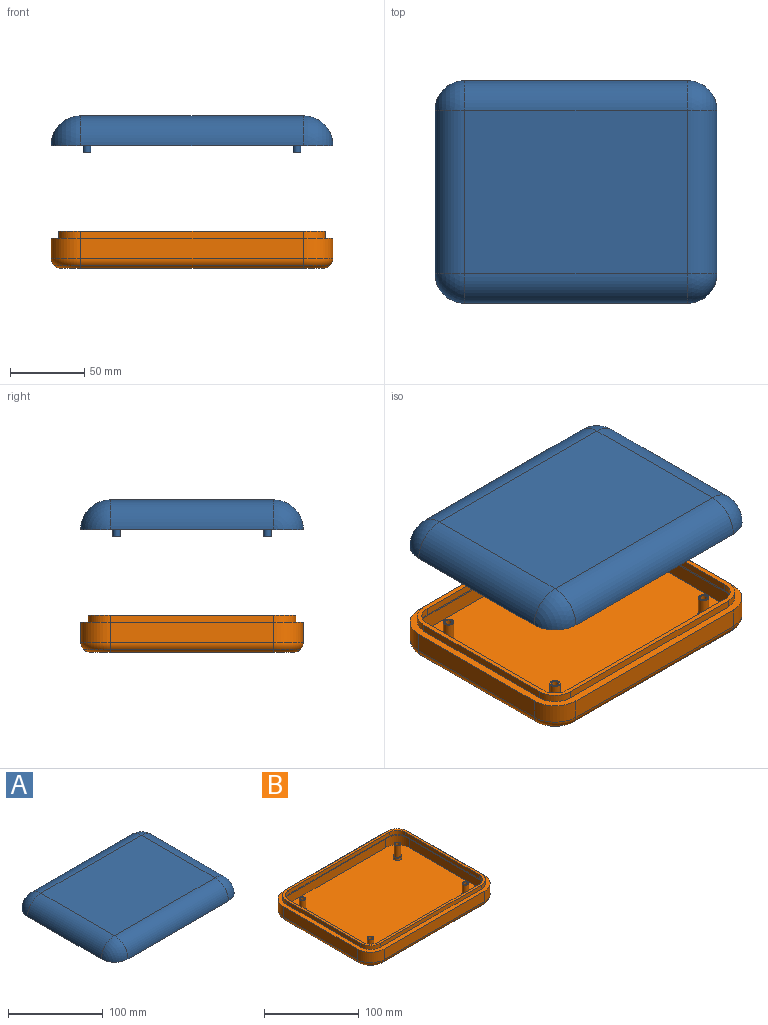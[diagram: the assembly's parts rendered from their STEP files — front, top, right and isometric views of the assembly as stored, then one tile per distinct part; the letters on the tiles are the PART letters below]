
ASSEMBLY  parts=2 mates=1
PART A: 43 faces, bbox 190x150x25 mm
  f0: plane 150x110mm, normal (0,0,-1), area 16346.1mm2, adj f3,f10,f16,f18,f19,f21,f23,f25
  f1: plane 150x110mm, normal (0,0,1), area 16500mm2, adj f6,f13,f15,f17
  f2: sphere r=15mm, area 353.4mm2, adj f3,f8,f16
  f3: cylinder r=15mm len=150mm, axis (-1,0,0), area 3534.3mm2, adj f0,f2,f4,f8
  f4: sphere r=15mm, area 353.4mm2, adj f3,f8,f18
  f5: sphere r=20mm, area 628.3mm2, adj f6,f8,f17
  f6: cylinder r=20mm len=150mm, axis (-1,0,0), area 4712.4mm2, adj f1,f5,f7,f8
  f7: sphere r=20mm, area 628.3mm2, adj f6,f8,f15
  f8: plane 190x150mm, normal (0,0,-1), area 3149.8mm2, adj f2,f3,f4,f5,f6,f7,f9,f10
  f9: sphere r=15mm, area 353.4mm2, adj f8,f10,f18
  f10: cylinder r=15mm len=150mm, axis (1,0,0), area 3534.3mm2, adj f0,f8,f9,f11
  f11: sphere r=15mm, area 353.4mm2, adj f8,f10,f16
  f12: sphere r=20mm, area 628.3mm2, adj f8,f13,f15
  f13: cylinder r=20mm len=150mm, axis (1,0,0), area 4712.4mm2, adj f1,f8,f12,f14
  f14: sphere r=20mm, area 628.3mm2, adj f8,f13,f17
  f15: cylinder r=20mm len=110mm, axis (0,1,0), area 3455.8mm2, adj f1,f7,f8,f12
  f16: cylinder r=15mm len=110mm, axis (0,1,0), area 2591.8mm2, adj f0,f2,f8,f11
  f17: cylinder r=20mm len=110mm, axis (0,-1,0), area 3455.8mm2, adj f1,f5,f8,f14
  f18: cylinder r=15mm len=110mm, axis (0,-1,0), area 2591.8mm2, adj f0,f4,f8,f9
  f19: cylinder r=3.5mm len=15mm, axis (0,0,1), area 329.9mm2, adj f0,f20
  f20: plane 7x7mm, normal (0,0,-1), area 18.8mm2, adj f19,f27
  f21: cylinder r=3.5mm len=15mm, axis (0,0,1), area 329.9mm2, adj f0,f22
  f22: plane 7x7mm, normal (0,0,-1), area 18.8mm2, adj f21,f32
  f23: cylinder r=3.5mm len=15mm, axis (0,0,1), area 329.9mm2, adj f0,f24
  f24: plane 7x7mm, normal (0,0,-1), area 18.8mm2, adj f23,f36
  f25: cylinder r=3.5mm len=15mm, axis (0,0,1), area 329.9mm2, adj f0,f26
  f26: plane 7x7mm, normal (0,0,-1), area 18.8mm2, adj f25,f40
  f27: cylinder r=2.5mm len=5mm, axis (0,0,1), area 78.5mm2, adj f20,f29
  f28: cylinder r=1.5mm len=20mm, axis (0,0,1), area 188.5mm2, adj f29,f30
  f29: plane 5x5mm, normal (0,0,-1), area 12.6mm2, adj f27,f28
  f30: plane 3x3mm, normal (0,0,-1), area 7.1mm2, adj f28
  f31: cylinder r=1.5mm len=20mm, axis (0,0,1), area 188.5mm2, adj f33,f34
  f32: cylinder r=2.5mm len=5mm, axis (0,0,1), area 78.5mm2, adj f22,f33
  f33: plane 5x5mm, normal (0,0,-1), area 12.6mm2, adj f31,f32
  f34: plane 3x3mm, normal (0,0,-1), area 7.1mm2, adj f31
  f35: cylinder r=1.5mm len=20mm, axis (0,0,1), area 188.5mm2, adj f37,f38
  f36: cylinder r=2.5mm len=5mm, axis (0,0,1), area 78.5mm2, adj f24,f37
  f37: plane 5x5mm, normal (0,0,-1), area 12.6mm2, adj f35,f36
  f38: plane 3x3mm, normal (0,0,-1), area 7.1mm2, adj f35
  f39: cylinder r=1.5mm len=20mm, axis (0,0,1), area 188.5mm2, adj f41,f42
  f40: cylinder r=2.5mm len=5mm, axis (0,0,1), area 78.5mm2, adj f26,f41
  f41: plane 5x5mm, normal (0,0,-1), area 12.6mm2, adj f39,f40
  f42: plane 3x3mm, normal (0,0,-1), area 7.1mm2, adj f39
PART B: 90 faces, bbox 193.3x153.3x25 mm
  f0: cylinder r=1.5mm len=12mm, axis (0,0,-1), area 113.1mm2, adj f35,f89
  f1: cylinder r=1.5mm len=12mm, axis (0,0,-1), area 113.1mm2, adj f37,f87
  f2: cylinder r=1.5mm len=12mm, axis (0,0,-1), area 113.1mm2, adj f39,f85
  f3: cylinder r=1.5mm len=12mm, axis (0,0,-1), area 113.1mm2, adj f41,f83
  f4: plane 7x7mm, normal (0,0,1), area 18.8mm2, adj f62,f88
  f5: plane 7x7mm, normal (0,0,1), area 18.8mm2, adj f65,f86
  f6: plane 7x7mm, normal (0,0,1), area 18.8mm2, adj f68,f84
  f7: plane 7x7mm, normal (0,0,1), area 18.8mm2, adj f71,f82
  f8: plane 190x150mm, normal (0,0,1), area 3149.8mm2, adj f9,f10,f11,f12,f13,f14,f15,f16
  f9: cylinder r=20mm len=20mm, axis (0,0,1), area 424.1mm2, adj f8,f10,f16,f79
  f10: plane 150x13.5mm, normal (0,-1,0), area 2025mm2, adj f8,f9,f11,f77
  f11: cylinder r=20mm len=20mm, axis (0,0,1), area 424.1mm2, adj f8,f10,f12,f75
  f12: plane 110x13.5mm, normal (1,0,0), area 1485mm2, adj f8,f11,f13,f74
  f13: cylinder r=20mm len=20mm, axis (0,0,1), area 424.1mm2, adj f8,f12,f14,f76
  f14: plane 150x13.5mm, normal (0,1,0), area 2025mm2, adj f8,f13,f15,f78
  f15: cylinder r=20mm len=20mm, axis (0,0,1), area 424.1mm2, adj f8,f14,f16,f80
  f16: plane 110x13.5mm, normal (-1,0,0), area 1485mm2, adj f8,f9,f15,f81
  f17: plane 177x137mm, normal (0,0,-1), area 24014mm2, adj f36,f38,f40,f42,f74,f75,f76,f77
  f18: plane 150x5mm, normal (0,1,0), area 750mm2, adj f19,f33,f34,f43
  f19: cylinder r=12mm len=12mm, axis (0,0,-1), area 94.2mm2, adj f18,f20,f34,f43
  f20: plane 110x5mm, normal (1,0,0), area 550mm2, adj f19,f21,f34,f43
  f21: cylinder r=12mm len=12mm, axis (0,0,-1), area 94.2mm2, adj f20,f22,f34,f43
  f22: plane 150x5mm, normal (0,-1,0), area 750mm2, adj f21,f23,f34,f43
  f23: cylinder r=12mm len=12mm, axis (0,0,-1), area 94.2mm2, adj f22,f24,f34,f43
  f24: plane 110x5mm, normal (-1,0,0), area 550mm2, adj f23,f33,f34,f43
  f25: cylinder r=15mm len=15mm, axis (0,0,-1), area 117.8mm2, adj f8,f26,f32,f34
  f26: plane 150x5mm, normal (0,-1,0), area 750mm2, adj f8,f25,f27,f34
  f27: cylinder r=15mm len=15mm, axis (0,0,-1), area 117.8mm2, adj f8,f26,f28,f34
  f28: plane 110x5mm, normal (1,0,0), area 550mm2, adj f8,f27,f29,f34
  f29: cylinder r=15mm len=15mm, axis (0,0,-1), area 117.8mm2, adj f8,f28,f30,f34
  f30: plane 150x5mm, normal (0,1,0), area 750mm2, adj f8,f29,f31,f34
  f31: cylinder r=15mm len=15mm, axis (0,0,-1), area 117.8mm2, adj f8,f30,f32,f34
  f32: plane 110x5mm, normal (-1,0,0), area 550mm2, adj f8,f25,f31,f34
  f33: cylinder r=12mm len=12mm, axis (0,0,-1), area 94.2mm2, adj f18,f24,f34,f43
  f34: plane 180x140mm, normal (0,0,1), area 1814.5mm2, adj f18,f19,f20,f21,f22,f23,f24,f25
  f35: plane 5x5mm, normal (0,0,-1), area 12.6mm2, adj f0,f36
  f36: cylinder r=2.5mm len=5mm, axis (0,0,-1), area 47.1mm2, adj f17,f35
  f37: plane 5x5mm, normal (0,0,-1), area 12.6mm2, adj f1,f38
  f38: cylinder r=2.5mm len=5mm, axis (0,0,-1), area 47.1mm2, adj f17,f37
  f39: plane 5x5mm, normal (0,0,-1), area 12.6mm2, adj f2,f40
  f40: cylinder r=2.5mm len=5mm, axis (0,0,-1), area 47.1mm2, adj f17,f39
  f41: plane 5x5mm, normal (0,0,-1), area 12.6mm2, adj f3,f42
  f42: cylinder r=2.5mm len=5mm, axis (0,0,-1), area 47.1mm2, adj f17,f41
  f43: plane 176x136mm, normal (0,0,-1), area 598.5mm2, adj f18,f19,f20,f21,f22,f23,f24,f33
  f44: plane 186x146mm, normal (0,0,-1), area 3086.9mm2, adj f45,f46,f47,f48,f49,f50,f51,f52
  f45: cylinder r=18mm len=18mm, axis (0,0,1), area 452.4mm2, adj f44,f46,f52,f53
  f46: plane 150x16mm, normal (0,1,0), area 2400mm2, adj f44,f45,f47,f53
  f47: cylinder r=18mm len=18mm, axis (0,0,1), area 452.4mm2, adj f44,f46,f48,f53
  f48: plane 110x16mm, normal (-1,0,0), area 1760mm2, adj f44,f47,f49,f53
  f49: cylinder r=18mm len=18mm, axis (0,0,1), area 452.4mm2, adj f44,f48,f50,f53
  f50: plane 150x16mm, normal (0,-1,0), area 2400mm2, adj f44,f49,f51,f53
  f51: cylinder r=18mm len=18mm, axis (0,0,1), area 452.4mm2, adj f44,f50,f52,f53
  f52: plane 110x16mm, normal (1,0,0), area 1760mm2, adj f44,f45,f51,f53
  f53: plane 186x146mm, normal (0,0,1), area 26623.4mm2, adj f45,f46,f47,f48,f49,f50,f51,f52
  f54: cylinder r=13mm len=13mm, axis (0,0,-1), area 40.8mm2, adj f43,f44,f55,f61
  f55: plane 150x2mm, normal (0,1,0), area 300mm2, adj f43,f44,f54,f56
  f56: cylinder r=13mm len=13mm, axis (0,0,-1), area 40.8mm2, adj f43,f44,f55,f57
  f57: plane 110x2mm, normal (-1,0,0), area 220mm2, adj f43,f44,f56,f58
  f58: cylinder r=13mm len=13mm, axis (0,0,-1), area 40.8mm2, adj f43,f44,f57,f59
  f59: plane 150x2mm, normal (0,-1,0), area 300mm2, adj f43,f44,f58,f60
  f60: cylinder r=13mm len=13mm, axis (0,0,-1), area 40.8mm2, adj f43,f44,f59,f61
  f61: plane 110x2mm, normal (1,0,0), area 220mm2, adj f43,f44,f54,f60
  f62: cylinder r=3.5mm len=15mm, axis (0,0,-1), area 329.9mm2, adj f4,f63
  f63: plane 9x9mm, normal (0,0,1), area 25.1mm2, adj f62,f64
  f64: cylinder r=4.5mm len=9mm, axis (0,0,-1), area 84.8mm2, adj f53,f63
  f65: cylinder r=3.5mm len=15mm, axis (0,0,-1), area 329.9mm2, adj f5,f66
  f66: plane 9x9mm, normal (0,0,1), area 25.1mm2, adj f65,f67
  f67: cylinder r=4.5mm len=9mm, axis (0,0,-1), area 84.8mm2, adj f53,f66
  f68: cylinder r=3.5mm len=15mm, axis (0,0,-1), area 329.9mm2, adj f6,f69
  f69: plane 9x9mm, normal (0,0,1), area 25.1mm2, adj f68,f70
  f70: cylinder r=4.5mm len=9mm, axis (0,0,-1), area 84.8mm2, adj f53,f69
  f71: cylinder r=3.5mm len=15mm, axis (0,0,-1), area 329.9mm2, adj f7,f72
  f72: plane 9x9mm, normal (0,0,1), area 25.1mm2, adj f71,f73
  f73: cylinder r=4.5mm len=9mm, axis (0,0,-1), area 84.8mm2, adj f53,f72
  f74: cylinder r=6.5mm len=110mm, axis (0,-1,0), area 1123.1mm2, adj f12,f17,f75,f76
  f75: torus R=13.5mm, axis (0,0,1), area 282.9mm2, adj f11,f17,f74,f77
  f76: torus R=13.5mm, axis (0,0,1), area 282.9mm2, adj f13,f17,f74,f78
  f77: cylinder r=6.5mm len=150mm, axis (-1,0,0), area 1531.5mm2, adj f10,f17,f75,f79
  f78: cylinder r=6.5mm len=150mm, axis (1,0,0), area 1531.5mm2, adj f14,f17,f76,f80
  f79: torus R=13.5mm, axis (0,0,1), area 282.9mm2, adj f9,f17,f77,f81
  f80: torus R=13.5mm, axis (0,0,1), area 282.9mm2, adj f15,f17,f78,f81
  f81: cylinder r=6.5mm len=110mm, axis (0,1,0), area 1123.1mm2, adj f16,f17,f79,f80
  f82: cylinder r=2.5mm len=5mm, axis (0,0,1), area 78.5mm2, adj f7,f83
  f83: plane 5x5mm, normal (0,0,1), area 12.6mm2, adj f3,f82
  f84: cylinder r=2.5mm len=5mm, axis (0,0,1), area 78.5mm2, adj f6,f85
  f85: plane 5x5mm, normal (0,0,1), area 12.6mm2, adj f2,f84
  f86: cylinder r=2.5mm len=5mm, axis (0,0,1), area 78.5mm2, adj f5,f87
  f87: plane 5x5mm, normal (0,0,1), area 12.6mm2, adj f1,f86
  f88: cylinder r=2.5mm len=5mm, axis (0,0,1), area 78.5mm2, adj f4,f89
  f89: plane 5x5mm, normal (0,0,1), area 12.6mm2, adj f0,f88
PLACE A rot(axis=(-0.17,0.99,0.01),0deg) t=(22.83,-41.86,212.64)mm
PLACE B t=(22.83,-41.86,150)mm
MATE slider B.f0 <-> A.f23  axis (0,0,1) through (-47.93,-92.62,125)mm
